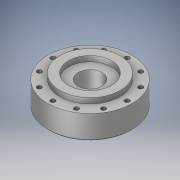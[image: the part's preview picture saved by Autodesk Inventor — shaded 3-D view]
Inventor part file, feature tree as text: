
AUTODESK INVENTOR PART (.ipt)
format: ipt  version: 2018 (Build 220112000, 112)  size: 218,624 bytes
history: native  units: in
note: dims shown in document units (in); Inventor stores cm internally (conversion verified against a paired STEP export)
features: sketch x6, extrude x5, chamfer x2, hole x1, pattern_circular x1
ambient origin geometry x8: Origin, YZ Plane, XZ Plane, XY Plane, X Axis, Y Axis, Z Axis, Center Point
bodies: Solid1 (feature_tree)
feature tree (15):
  extrude  "Extrusion1"  Depth=0.5in TaperAngle=0.0deg
  chamfer  "Chamfer1"  Distance=0.0291in Angle=45.0deg
  extrude  "Extrusion2"  Depth=0.113in TaperAngle=0.0deg
  extrude  "Extrusion3"  Depth=0.05in
  hole  "Hole1"  [1 undecoded]
  chamfer  "Chamfer3"  Distance=0.007in Angle=45.0deg
  extrude  "Extrusion6"  Depth=0.5in
  pattern_circular  "Circular Pattern2"  [2 undecoded]
  sketch  "Sketch1"  dims[d0=1.755in d1=0.5in d2=0.0in d3=0.0291in d4=0.125in d5=45.0deg]
  sketch  "Sketch2"  dims[d6=1.26in d7=0.113in d8=0.0in]
  sketch  "Sketch3"  dims[d9=0.658in d10=0.05in]
  sketch  "Sketch6"  dims[d11=0.04in d12=0.0in d22=0.775in]
  sketch  "Sketch7"  dims[d23=30.0deg]
  sketch  "Sketch9"  dims[d24=0.085in d25=0.224in d26=0.375in d27=0.25in d28=0.5635in d29=0.349in d30=0.8108in d31=0.007in d32=0.125in d33=45.0deg d37=0.9in d38=1.0in d39=0.0in d45=0.5in d47=0.0in d48=0.04in d52=4.7244in d53=360.0deg]
  extrude  "Extrusion8"  Depth=0.5in TaperAngle=0.0deg
note: 3 required parameter values undecoded (feature->parameter linkage not recoverable at this tier; creation-order binding heuristic only, values carry confidence <= 0.55)
